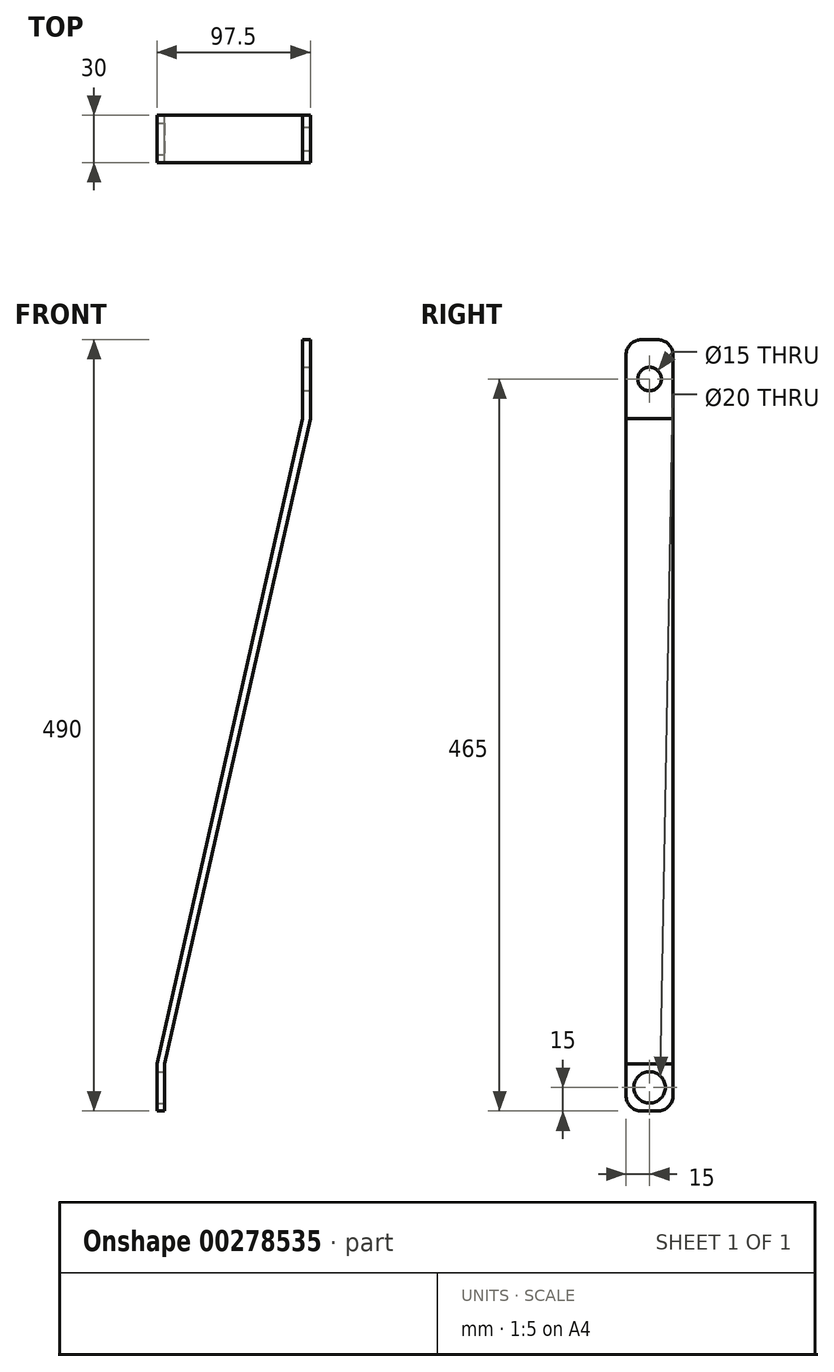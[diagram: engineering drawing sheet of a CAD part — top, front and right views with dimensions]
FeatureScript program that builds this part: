
annotation { "Feature Type Name" : "Feature", "Feature Type Description" : "" }
export const myFeature = defineFeature(function(context is Context, id is Id, definition is map)
    precondition{}
    {
        {
            var Q0;
            Q0=qCreatedBy(makeId("Front.planeOp"),FACE);
            var sketch = newSketch(context, id + "F0", { "sketchPlane" : qUnion([Q0])});
            skLineSegment(sketch, "E0", {"start": v(0, 0) * mm, "end": v(0, 50) * mm});
            skLineSegment(sketch, "E1", {"start": v(0, 50) * mm, "end": v(5, 50) * mm});
            skLineSegment(sketch, "E2", {"start": v(5, 50) * mm, "end": v(5, 0) * mm});
            skLineSegment(sketch, "E3", {"start": v(5, 0) * mm, "end": v(-87.5, -410) * mm});
            skLineSegment(sketch, "E4", {"start": v(-87.5, -410) * mm, "end": v(-87.5, -440) * mm});
            skLineSegment(sketch, "E5", {"start": v(-87.5, -440) * mm, "end": v(-92.5, -440) * mm});
            skLineSegment(sketch, "E6", {"start": v(-92.5, -440) * mm, "end": v(-92.5, -410) * mm});
            skLineSegment(sketch, "E7", {"start": v(-92.5, -410) * mm, "end": v(0, 0) * mm});
            skLineSegment(sketch, "E8", {"start": v(-150, 76.67) * mm, "end": v(-150, -369.79) * mm, "construction": true});
            skPoint(sketch, "E9", {"position": v(0, 25) * mm});
            skPoint(sketch, "E10", {"position": v(-92.5, -425) * mm});
            skSolve(sketch);
        }
        {
            var Q0;
            Q0=makeQuery(id+"F0.imprint","IMPRINT",FACE,{"disambiguationData":[TD([[makeQuery(id+"F0.imprint","IMPRINT",EDGE,{"derivedFrom":sQuery(id+"F0.wireOp",EDGE,"E0")}),-1.0]])]});
            extrude(context, id + "F1", {"entities" : qUnion([Q0]), "depth" : 30 * mm});
        }
        {
            var Q0;
            Q0=makeQuery(id+"F1.opExtrude","SWEPT_FACE",FACE,{"disambiguationData":[OSD([sQuery(id+"F0.wireOp",EDGE,"E2")])]});
            var sketch = newSketch(context, id + "F2", { "sketchPlane" : qUnion([Q0])});
            skCircle(sketch, "E11", {"center": v(-15, 25) * mm, "radius": 7.5 * mm});
            skPoint(sketch, "E11.centerSnap0", {"position": v(0, 25) * mm});
            skSolve(sketch);
        }
        {
            var Q0;
            Q0 = qSketchRegion(id + "F2", true);
            extrude(context, id + "F3", {"entities" : qUnion([Q0]), "operationType" : NewBodyOperationType.REMOVE, "endBound" : BoundingType.THROUGH_ALL, "oppositeDirection" : true, "depth" : 25 * mm});
        }
        {
            var Q0;
            Q0=makeQuery(id+"F1.opExtrude","SWEPT_FACE",FACE,{"disambiguationData":[OSD([sQuery(id+"F0.wireOp",EDGE,"E4")])]});
            var sketch = newSketch(context, id + "F4", { "sketchPlane" : qUnion([Q0])});
            skCircle(sketch, "E12", {"center": v(-15, -425) * mm, "radius": 10 * mm});
            skPoint(sketch, "E12.centerSnap0", {"position": v(-15, -410) * mm});
            skSolve(sketch);
        }
        {
            var Q0;
            Q0 = qSketchRegion(id + "F4", true);
            extrude(context, id + "F5", {"entities" : qUnion([Q0]), "operationType" : NewBodyOperationType.REMOVE, "endBound" : BoundingType.THROUGH_ALL, "oppositeDirection" : true, "depth" : 25 * mm});
        }
        {
            var Q0;
            Q0=makeQuery(id+"F1.opExtrude","CAP_EDGE",EDGE,{"disambiguationData":[OSD([sQuery(id+"F0.wireOp",EDGE,"E5")])],"isStart":false});
            var Q1;
            Q1=makeQuery(id+"F1.opExtrude","CAP_EDGE",EDGE,{"disambiguationData":[OSD([sQuery(id+"F0.wireOp",EDGE,"E5")])],"isStart":true});
            var Q2;
            Q2=makeQuery(id+"F1.opExtrude","CAP_EDGE",EDGE,{"disambiguationData":[OSD([sQuery(id+"F0.wireOp",EDGE,"E1")])],"isStart":false});
            var Q3;
            Q3=makeQuery(id+"F1.opExtrude","CAP_EDGE",EDGE,{"disambiguationData":[OSD([sQuery(id+"F0.wireOp",EDGE,"E1")])],"isStart":true});
            fillet(context, id + "F6", {"entities" : qUnion([Q0, Q1, Q2, Q3]), "radius" : 10 * mm, "tangentPropagation" : true, "allowEdgeOverflow" : false});
        }
    });
